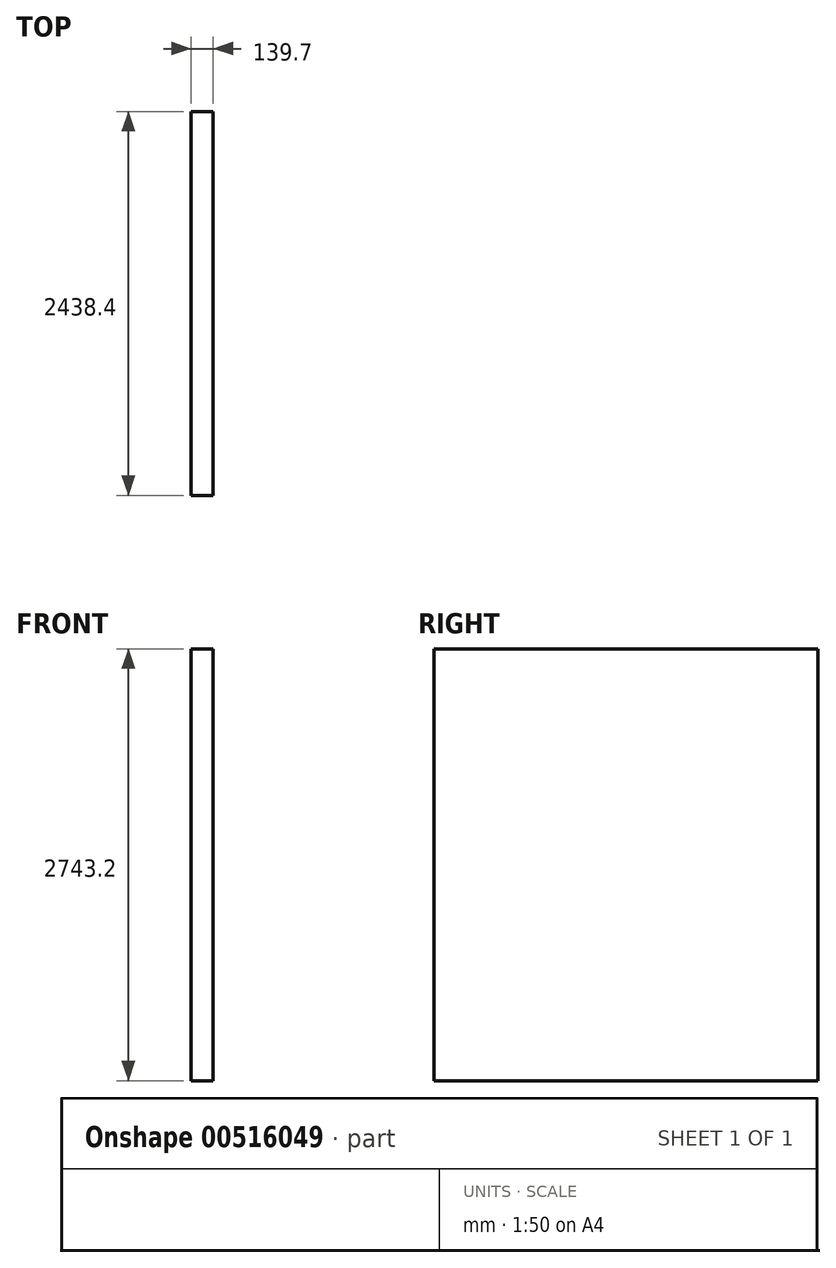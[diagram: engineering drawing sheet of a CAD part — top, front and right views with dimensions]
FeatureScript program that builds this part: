
annotation { "Feature Type Name" : "Feature", "Feature Type Description" : "" }
export const myFeature = defineFeature(function(context is Context, id is Id, definition is map)
    precondition{}
    {
        {
            var Q0;
            Q0=qCreatedBy(makeId("Right.planeOp"),FACE);
            var sketch = newSketch(context, id + "F0", { "sketchPlane" : qUnion([Q0])});
            skLineSegment(sketch, "E0.bottom", {"start": v(1219.2, -1371.6) * mm, "end": v(-1219.2, -1371.6) * mm});
            skLineSegment(sketch, "E0.top", {"start": v(1219.2, 1371.6) * mm, "end": v(-1219.2, 1371.6) * mm});
            skLineSegment(sketch, "E0.left", {"start": v(1219.2, -1371.6) * mm, "end": v(1219.2, 1371.6) * mm});
            skLineSegment(sketch, "E0.right", {"start": v(-1219.2, -1371.6) * mm, "end": v(-1219.2, 1371.6) * mm});
            skPoint(sketch, "E0.middle", {"position": v(0, 0) * mm});
            skSolve(sketch);
        }
        {
            var Q0;
            Q0=makeQuery(id+"F0.imprint","IMPRINT",FACE,{"disambiguationData":[TD([[makeQuery(id+"F0.imprint","IMPRINT",EDGE,{"derivedFrom":sQuery(id+"F0.wireOp",EDGE,"E0.bottom")}),-1.0]])]});
            extrude(context, id + "F1", {"entities" : qUnion([Q0]), "depth" : 139.7 * mm, "offsetDistance" : 25.4 * mm});
        }
    });
